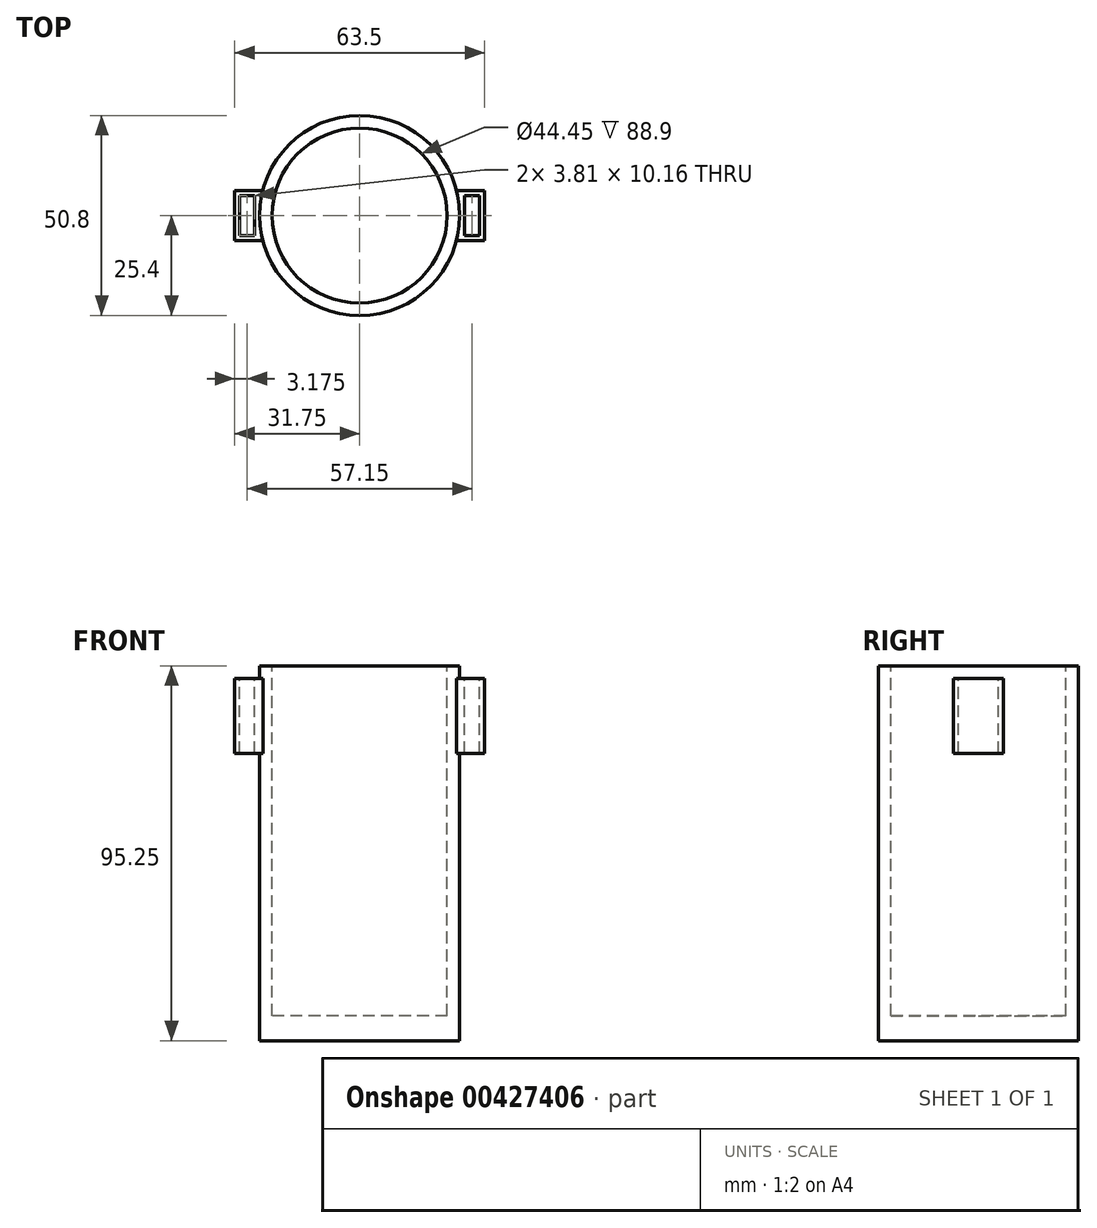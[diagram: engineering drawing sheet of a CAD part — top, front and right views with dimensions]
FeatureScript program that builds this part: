
annotation { "Feature Type Name" : "Feature", "Feature Type Description" : "" }
export const myFeature = defineFeature(function(context is Context, id is Id, definition is map)
    precondition{}
    {
        {
            var Q0;
            Q0=qCreatedBy(makeId("Top.planeOp"),FACE);
            var sketch = newSketch(context, id + "F0", { "sketchPlane" : qUnion([Q0])});
            skLineSegment(sketch, "E0.bottom", {"start": v(25.4, -25.4) * mm, "end": v(-25.4, -25.4) * mm});
            skLineSegment(sketch, "E0.top", {"start": v(25.4, 25.4) * mm, "end": v(-25.4, 25.4) * mm});
            skLineSegment(sketch, "E0.left", {"start": v(25.4, -25.4) * mm, "end": v(25.4, 25.4) * mm});
            skLineSegment(sketch, "E0.right", {"start": v(-25.4, -25.4) * mm, "end": v(-25.4, 25.4) * mm});
            skPoint(sketch, "E0.middle", {"position": v(0, 0) * mm});
            skSolve(sketch);
        }
        {
            var Q0;
            Q0 = qSketchRegion(id + "F0", true);
            extrude(context, id + "F1", {"entities" : qUnion([Q0]), "depth" : 95.25 * mm});
        }
        {
            var Q0;
            Q0=makeQuery(id+"F1.opExtrude","SWEPT_FACE",FACE,{"disambiguationData":[OSD([sQuery(id+"F0.wireOp",EDGE,"E0.right")])]});
            var sketch = newSketch(context, id + "F2", { "sketchPlane" : qUnion([Q0])});
            skLineSegment(sketch, "E1", {"start": v(-25.4, 95.25) * mm, "end": v(0, 95.25) * mm});
            skLineSegment(sketch, "E2", {"start": v(0, 95.25) * mm, "end": v(0, 82.55) * mm});
            skLineSegment(sketch, "E3.bottom", {"start": v(6.35, 73.03) * mm, "end": v(-6.35, 73.03) * mm});
            skLineSegment(sketch, "E3.top", {"start": v(6.35, 92.08) * mm, "end": v(-6.35, 92.08) * mm});
            skLineSegment(sketch, "E3.left", {"start": v(6.35, 73.03) * mm, "end": v(6.35, 92.08) * mm});
            skLineSegment(sketch, "E3.right", {"start": v(-6.35, 73.03) * mm, "end": v(-6.35, 92.08) * mm});
            skPoint(sketch, "E3.middle", {"position": v(0, 82.55) * mm});
            skSolve(sketch);
        }
        {
            var Q0;
            Q0 = qSketchRegion(id + "F2", true);
            extrude(context, id + "F3", {"entities" : qUnion([Q0]), "operationType" : NewBodyOperationType.ADD, "depth" : 6.35 * mm});
        }
        {
            var Q0;
            Q0=makeQuery(id+"F1.opExtrude","SWEPT_BODY",BODY,{"disambiguationData":[OSD([sQuery(id+"F0.wireOp",EDGE,"E0.bottom"),sQuery(id+"F0.wireOp",EDGE,"E0.top"),sQuery(id+"F0.wireOp",EDGE,"E0.left"),sQuery(id+"F0.wireOp",EDGE,"E0.right")])]});
            var Q1;
            Q1=qCreatedBy(makeId("Right.planeOp"),FACE);
            mirror(context, id + "F4", {"operationType" : NewBodyOperationType.ADD, "entities" : qUnion([Q0]), "mirrorPlane" : qUnion([Q1])});
        }
        {
            var Q0;
            Q0=makeQuery(id+"F1.opExtrude","CAP_FACE",FACE,{"disambiguationData":[OSD([sQuery(id+"F0.wireOp",EDGE,"E0.bottom"),sQuery(id+"F0.wireOp",EDGE,"E0.top"),sQuery(id+"F0.wireOp",EDGE,"E0.left"),sQuery(id+"F0.wireOp",EDGE,"E0.right")])],"isStart":false});
            var sketch = newSketch(context, id + "F5", { "sketchPlane" : qUnion([Q0])});
            skLineSegment(sketch, "E4", {"start": v(-25.4, 0) * mm, "end": v(-31.75, 0) * mm});
            skLineSegment(sketch, "E5", {"start": v(-31.75, 0) * mm, "end": v(-28.58, 0) * mm});
            skLineSegment(sketch, "E6.bottom", {"start": v(-26.67, -5.08) * mm, "end": v(-30.48, -5.08) * mm});
            skLineSegment(sketch, "E6.top", {"start": v(-26.67, 5.08) * mm, "end": v(-30.48, 5.08) * mm});
            skLineSegment(sketch, "E6.left", {"start": v(-26.67, -5.08) * mm, "end": v(-26.67, 5.08) * mm});
            skLineSegment(sketch, "E6.right", {"start": v(-30.48, -5.08) * mm, "end": v(-30.48, 5.08) * mm});
            skPoint(sketch, "E6.middle", {"position": v(-28.58, 0) * mm});
            skLineSegment(sketch, "E7.MirrorCS", {"start": v(30.48, -5.08) * mm, "end": v(30.48, 5.08) * mm});
            skLineSegment(sketch, "E8.MirrorCS", {"start": v(26.67, -5.08) * mm, "end": v(30.48, -5.08) * mm});
            skLineSegment(sketch, "E9.MirrorCS", {"start": v(26.67, -5.08) * mm, "end": v(26.67, 5.08) * mm});
            skLineSegment(sketch, "E10.MirrorCS", {"start": v(26.67, 5.08) * mm, "end": v(30.48, 5.08) * mm});
            skSolve(sketch);
        }
        {
            var Q0;
            Q0 = qSketchRegion(id + "F5", true);
            extrude(context, id + "F6", {"entities" : qUnion([Q0]), "operationType" : NewBodyOperationType.REMOVE, "oppositeDirection" : true, "depth" : 25.4 * mm});
        }
        {
            var Q0;
            Q0=makeQuery(id+"F1.opExtrude","SWEPT_EDGE",EDGE,{"disambiguationData":[OSD([sQuery(id+"F0.wireOp",EDGE,"E0.bottom"),sQuery(id+"F0.wireOp",EDGE,"E0.right")])]});
            var Q1;
            Q1=makeQuery(id+"F1.opExtrude","SWEPT_EDGE",EDGE,{"disambiguationData":[OSD([sQuery(id+"F0.wireOp",EDGE,"E0.bottom"),sQuery(id+"F0.wireOp",EDGE,"E0.left")])]});
            var Q2;
            Q2=makeQuery(id+"F1.opExtrude","SWEPT_EDGE",EDGE,{"disambiguationData":[OSD([sQuery(id+"F0.wireOp",EDGE,"E0.top"),sQuery(id+"F0.wireOp",EDGE,"E0.left")])]});
            var Q3;
            Q3=makeQuery(id+"F1.opExtrude","SWEPT_EDGE",EDGE,{"disambiguationData":[OSD([sQuery(id+"F0.wireOp",EDGE,"E0.top"),sQuery(id+"F0.wireOp",EDGE,"E0.right")])]});
            fillet(context, id + "F7", {"entities" : qUnion([Q0, Q1, Q2, Q3]), "radius" : 25.4 * mm, "tangentPropagation" : true, "allowEdgeOverflow" : false});
        }
        {
            var Q0;
            Q0=makeQuery(id+"F1.opExtrude","CAP_FACE",FACE,{"disambiguationData":[OSD([sQuery(id+"F0.wireOp",EDGE,"E0.bottom"),sQuery(id+"F0.wireOp",EDGE,"E0.top"),sQuery(id+"F0.wireOp",EDGE,"E0.left"),sQuery(id+"F0.wireOp",EDGE,"E0.right")])],"isStart":false});
            var sketch = newSketch(context, id + "F8", { "sketchPlane" : qUnion([Q0])});
            skCircle(sketch, "E11", {"center": v(0, 0) * mm, "radius": 22.23 * mm});
            skSolve(sketch);
        }
        {
            var Q0;
            Q0 = qSketchRegion(id + "F8", true);
            extrude(context, id + "F9", {"entities" : qUnion([Q0]), "operationType" : NewBodyOperationType.REMOVE, "depth" : -88.9 * mm});
        }
    });
